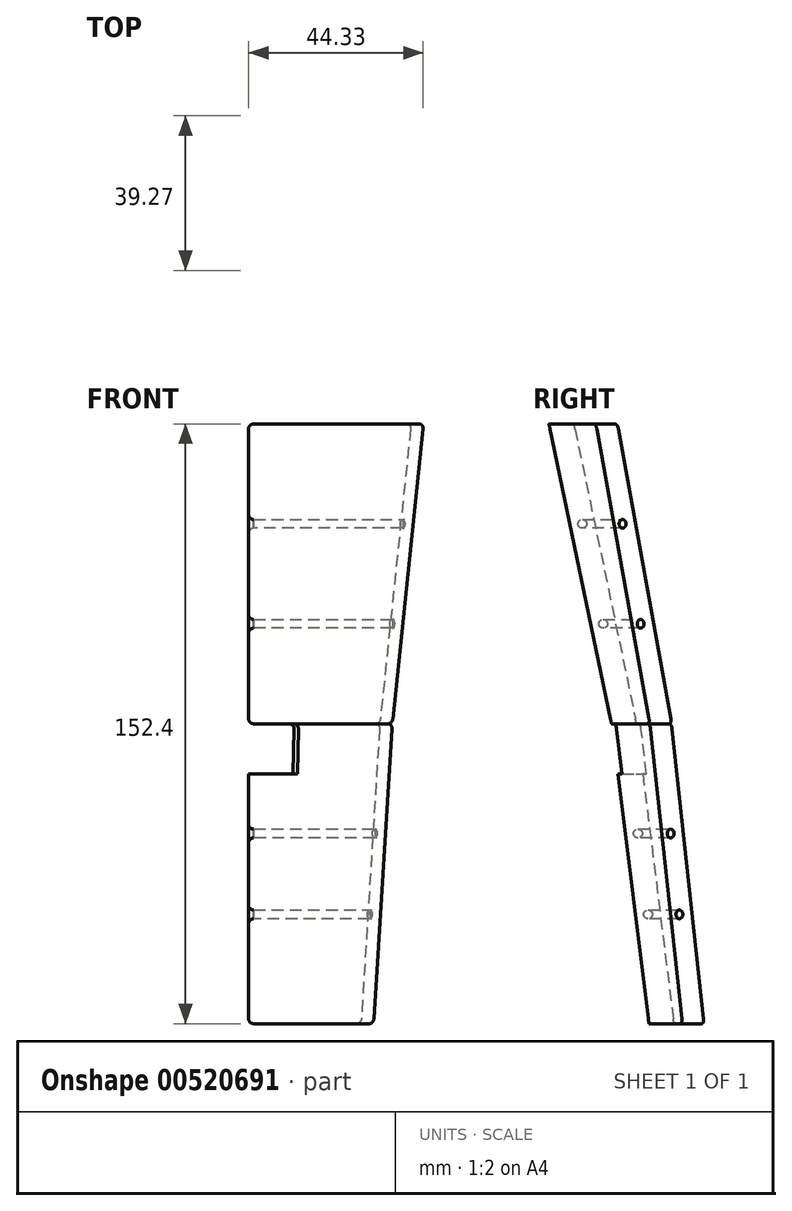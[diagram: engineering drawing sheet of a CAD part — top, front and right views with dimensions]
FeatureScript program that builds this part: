
annotation { "Feature Type Name" : "Feature", "Feature Type Description" : "" }
export const myFeature = defineFeature(function(context is Context, id is Id, definition is map)
    precondition{}
    {
        {
            var Q0;
            Q0=qCreatedBy(makeId("Right.planeOp"),FACE);
            var sketch = newSketch(context, id + "F0", { "sketchPlane" : qUnion([Q0])});
            skLineSegment(sketch, "E0", {"start": v(0, 0) * mm, "end": v(-63.5, 0) * mm});
            skLineSegment(sketch, "E1", {"start": v(0, 0) * mm, "end": v(0, 76.2) * mm});
            skLineSegment(sketch, "E2", {"start": v(0, 76.2) * mm, "end": v(-73.03, 76.2) * mm});
            skLineSegment(sketch, "E3", {"start": v(-73.03, 76.2) * mm, "end": v(-63.5, 0) * mm});
            skSolve(sketch);
        }
        {
            var Q0;
            Q0=makeQuery(id+"F0.imprint","IMPRINT",FACE,{"disambiguationData":[TD([[makeQuery(id+"F0.imprint","IMPRINT",EDGE,{"derivedFrom":sQuery(id+"F0.wireOp",EDGE,"E0")}),-1.0]])]});
            var Q1;
            Q1 = qSketchRegion(id + "F2", true);
            var Q2;
            Q2 = qSketchRegion(id + "F3", true);
            var Q3;
            Q3=sQuery(id+"F0.wireOp",EDGE,"E1");
            revolve(context, id + "F1", {"entities" : qUnion([Q0, Q1, Q2]), "axis" : qUnion([Q3]), "revolveType" : RevolveType.ONE_DIRECTION, "angle" : 30 * degree});
        }
        {
            var Q0;
            Q0=qCreatedBy(makeId("Right.planeOp"),FACE);
            var sketch = newSketch(context, id + "F2", { "sketchPlane" : qUnion([Q0])});
            skLineSegment(sketch, "E4", {"start": v(0, 0) * mm, "end": v(-57.15, 0) * mm});
            skLineSegment(sketch, "E5", {"start": v(0, 0) * mm, "end": v(0, 76.2) * mm});
            skLineSegment(sketch, "E6", {"start": v(-66.68, 76.2) * mm, "end": v(-57.15, 0) * mm});
            skLineSegment(sketch, "E7", {"start": v(-66.68, 76.2) * mm, "end": v(0, 76.2) * mm});
            skSolve(sketch);
        }
        {
            var Q0;
            Q0=qCreatedBy(makeId("Right.planeOp"),FACE);
            var sketch = newSketch(context, id + "F3", { "sketchPlane" : qUnion([Q0])});
            skLineSegment(sketch, "E8", {"start": v(0, 76.2) * mm, "end": v(-73.03, 76.2) * mm});
            skLineSegment(sketch, "E9", {"start": v(0, 76.2) * mm, "end": v(0, 63.5) * mm});
            skLineSegment(sketch, "E10", {"start": v(0, 63.5) * mm, "end": v(-71.44, 63.5) * mm});
            skLineSegment(sketch, "E11", {"start": v(-73.03, 76.2) * mm, "end": v(-71.44, 63.5) * mm});
            skSolve(sketch);
        }
        {
            var Q0;
            Q0 = qSketchRegion(id + "F2", true);
            var Q1;
            Q1=sQuery(id+"F2.wireOp",EDGE,"E5");
            revolve(context, id + "F4", {"operationType" : NewBodyOperationType.REMOVE, "entities" : qUnion([Q0]), "axis" : qUnion([Q1]), "revolveType" : RevolveType.FULL, "oppositeDirection" : true});
        }
        {
            var Q0;
            Q0=makeQuery(id+"F3.imprint","IMPRINT",FACE,{"disambiguationData":[TD([[makeQuery(id+"F3.imprint","IMPRINT",EDGE,{"derivedFrom":sQuery(id+"F3.wireOp",EDGE,"E8")}),1.0]])]});
            var Q1;
            Q1=sQuery(id+"F3.wireOp",EDGE,"E9");
            revolve(context, id + "F5", {"operationType" : NewBodyOperationType.REMOVE, "entities" : qUnion([Q0]), "axis" : qUnion([Q1]), "revolveType" : RevolveType.ONE_DIRECTION, "oppositeDirection" : true, "angle" : 20 * degree});
        }
        {
            var Q0;
            Q0 = qSketchRegion(id + "F3", true);
            var Q1;
            Q1=sQuery(id+"F3.wireOp",EDGE,"E9");
            revolve(context, id + "F6", {"operationType" : NewBodyOperationType.ADD, "entities" : qUnion([Q0]), "axis" : qUnion([Q1]), "revolveType" : RevolveType.ONE_DIRECTION, "oppositeDirection" : true, "angle" : 10 * degree});
        }
        {
            var Q0;
            Q0=qCreatedBy(makeId("Right.planeOp"),FACE);
            var sketch = newSketch(context, id + "F7", { "sketchPlane" : qUnion([Q0])});
            skLineSegment(sketch, "E12", {"start": v(0, 76.2) * mm, "end": v(-66.68, 76.2) * mm});
            skPoint(sketch, "E13", {"position": v(0, 63.5) * mm});
            skLineSegment(sketch, "E14", {"start": v(0, 63.5) * mm, "end": v(-65.09, 63.5) * mm});
            skLineSegment(sketch, "E15", {"start": v(0, 76.2) * mm, "end": v(0, 63.5) * mm});
            skLineSegment(sketch, "E16", {"start": v(-65.09, 63.5) * mm, "end": v(-66.68, 76.2) * mm});
            skSolve(sketch);
        }
        {
            var Q0;
            Q0 = qSketchRegion(id + "F7", true);
            var Q1;
            Q1=sQuery(id+"F3.wireOp",EDGE,"E9");
            revolve(context, id + "F8", {"operationType" : NewBodyOperationType.REMOVE, "entities" : qUnion([Q0]), "axis" : qUnion([Q1]), "revolveType" : RevolveType.FULL, "oppositeDirection" : true});
        }
        {
            var Q0;
            Q0=makeQuery(id+"F6.opRevolve","CAP_EDGE",EDGE,{"disambiguationData":[OSD([sQuery(id+"F3.wireOp",EDGE,"E8")])],"isStart":true});
            var Q1;
            Q1=makeQuery(id+"F6.opRevolve","CAP_EDGE",EDGE,{"disambiguationData":[OSD([sQuery(id+"F3.wireOp",EDGE,"E8")])],"isStart":false});
            var Q2;
            Q2=makeQuery(id+"F5.boolean.opBoolean","COPY",EDGE,{"derivedFrom":makeQuery(id+"F5.opRevolve","CAP_EDGE",EDGE,{"disambiguationData":[OSD([sQuery(id+"F3.wireOp",EDGE,"E8")])],"isStart":false})});
            var Q3;
            Q3=makeQuery(id+"F1.opRevolve","CAP_EDGE",EDGE,{"disambiguationData":[OSD([sQuery(id+"F0.wireOp",EDGE,"E2")])],"isStart":false});
            var Q4;
            Q4=makeQuery(id+"F5.boolean.opBoolean","COPY",EDGE,{"derivedFrom":makeQuery(id+"F5.opRevolve","CAP_EDGE",EDGE,{"disambiguationData":[OSD([sQuery(id+"F3.wireOp",EDGE,"E10")])],"isStart":false})});
            var Q5;
            {var subQ0=sQuery(id+"F3.wireOp",EDGE,"E10");Q5=makeQuery(id+"F6.boolean.opBoolean","SPLIT",EDGE,{"disambiguationData":[topologyDisambiguationEdgeConnected([makeQuery(id+"F5.boolean.opBoolean","COPY",FACE,{"derivedFrom":makeQuery(id+"F5.opRevolve","SWEPT_FACE",FACE,{"disambiguationData":[OSD([subQ0])]})})])],"derivedFrom":makeQuery(id+"F6.opRevolve","CAP_EDGE",EDGE,{"disambiguationData":[OSD([subQ0])],"isStart":false})});}
            var Q6;
            Q6=makeQuery(id+"F1.opRevolve","CAP_EDGE",EDGE,{"disambiguationData":[OSD([sQuery(id+"F0.wireOp",EDGE,"E0")])],"isStart":false});
            var Q7;
            Q7=makeQuery(id+"F1.opRevolve","CAP_EDGE",EDGE,{"disambiguationData":[OSD([sQuery(id+"F0.wireOp",EDGE,"E0")])],"isStart":true});
            fillet(context, id + "F9", {"entities" : qUnion([Q0, Q1, Q2, Q3, Q4, Q5, Q6, Q7]), "radius" : 1.27 * mm, "tangentPropagation" : true, "allowEdgeOverflow" : false});
        }
        {
            var Q0;
            Q0=qCreatedBy(makeId("Right.planeOp"),FACE);
            var sketch = newSketch(context, id + "F10", { "sketchPlane" : qUnion([Q0])});
            skLineSegment(sketch, "E17", {"start": v(0, 76.2) * mm, "end": v(0, 152.4) * mm});
            skLineSegment(sketch, "E18", {"start": v(0, 152.4) * mm, "end": v(-88.9, 152.4) * mm});
            skLineSegment(sketch, "E19", {"start": v(0, 76.2) * mm, "end": v(-73.03, 76.2) * mm});
            skLineSegment(sketch, "E20", {"start": v(-88.9, 152.4) * mm, "end": v(-73.03, 76.2) * mm});
            skSolve(sketch);
        }
        {
            var Q0;
            Q0 = qSketchRegion(id + "F10", true);
            var Q1;
            Q1=sQuery(id+"F10.wireOp",EDGE,"E17");
            revolve(context, id + "F11", {"entities" : qUnion([Q0]), "axis" : qUnion([Q1]), "revolveType" : RevolveType.ONE_DIRECTION, "angle" : 30 * degree});
        }
        {
            var Q0;
            Q0=qCreatedBy(makeId("Right.planeOp"),FACE);
            var sketch = newSketch(context, id + "F12", { "sketchPlane" : qUnion([Q0])});
            skLineSegment(sketch, "E21", {"start": v(0, 0) * mm, "end": v(0, 76.2) * mm});
            skLineSegment(sketch, "E22", {"start": v(0, 76.2) * mm, "end": v(0, 152.4) * mm});
            skLineSegment(sketch, "E23", {"start": v(0, 152.4) * mm, "end": v(-82.55, 152.4) * mm});
            skLineSegment(sketch, "E24", {"start": v(0, 76.2) * mm, "end": v(-66.68, 76.2) * mm});
            skLineSegment(sketch, "E25", {"start": v(-66.68, 76.2) * mm, "end": v(-82.55, 152.4) * mm});
            skSolve(sketch);
        }
        {
            var Q0;
            Q0 = qSketchRegion(id + "F12", true);
            var Q1;
            Q1=sQuery(id+"F12.wireOp",EDGE,"E22");
            revolve(context, id + "F13", {"operationType" : NewBodyOperationType.REMOVE, "entities" : qUnion([Q0]), "axis" : qUnion([Q1]), "revolveType" : RevolveType.FULL, "oppositeDirection" : true});
        }
        {
            var Q0;
            Q0=qCreatedBy(makeId("Right.planeOp"),FACE);
            var sketch = newSketch(context, id + "F14", { "sketchPlane" : qUnion([Q0])});
            skLineSegment(sketch, "E26", {"start": v(-71.44, 63.5) * mm, "end": v(-65.09, 63.5) * mm});
            skLineSegment(sketch, "E27", {"start": v(-65.09, 63.5) * mm, "end": v(-66.68, 76.2) * mm});
            skLineSegment(sketch, "E28", {"start": v(-73.03, 76.2) * mm, "end": v(-71.44, 63.5) * mm});
            skLineSegment(sketch, "E29", {"start": v(-73.03, 76.2) * mm, "end": v(-66.68, 76.2) * mm});
            skLineSegment(sketch, "E30", {"start": v(-65.09, 63.5) * mm, "end": v(-71.44, 63.5) * mm});
            skSolve(sketch);
        }
        {
            var Q0;
            Q0=qCreatedBy(makeId("Right.planeOp"),FACE);
            var sketch = newSketch(context, id + "F15", { "sketchPlane" : qUnion([Q0])});
            skLineSegment(sketch, "E31", {"start": v(0, 0) * mm, "end": v(0, 76) * mm});
            skSolve(sketch);
        }
        {
            var Q0;
            Q0=makeQuery(id+"F14.imprint","IMPRINT",FACE,{"disambiguationData":[TD([[makeQuery(id+"F14.imprint","IMPRINT",EDGE,{"derivedFrom":sQuery(id+"F14.wireOp",EDGE,"E27")}),1.0]])]});
            var Q1;
            Q1=sQuery(id+"F15.wireOp",EDGE,"E31");
            revolve(context, id + "F16", {"operationType" : NewBodyOperationType.ADD, "entities" : qUnion([Q0]), "axis" : qUnion([Q1]), "revolveType" : RevolveType.ONE_DIRECTION, "angle" : 20 * degree});
        }
        {
            var Q0;
            Q0 = qSketchRegion(id + "F14", true);
            var Q1;
            Q1=sQuery(id+"F15.wireOp",EDGE,"E31");
            revolve(context, id + "F17", {"operationType" : NewBodyOperationType.REMOVE, "entities" : qUnion([Q0]), "axis" : qUnion([Q1]), "revolveType" : RevolveType.ONE_DIRECTION, "angle" : 10 * degree});
        }
        {
            var Q0;
            Q0=makeQuery(id+"F16.opRevolve","CAP_EDGE",EDGE,{"disambiguationData":[OSD([sQuery(id+"F14.wireOp",EDGE,"E30")])],"isStart":false});
            var Q1;
            Q1=makeQuery(id+"F17.boolean.opBoolean","COPY",EDGE,{"derivedFrom":makeQuery(id+"F17.opRevolve","CAP_EDGE",EDGE,{"disambiguationData":[OSD([sQuery(id+"F14.wireOp",EDGE,"E30")])],"isStart":false})});
            var Q2;
            Q2=makeQuery(id+"F17.boolean.opBoolean","COPY",EDGE,{"derivedFrom":makeQuery(id+"F17.opRevolve","CAP_EDGE",EDGE,{"disambiguationData":[OSD([sQuery(id+"F14.wireOp",EDGE,"E29")])],"isStart":false})});
            var Q3;
            Q3=makeQuery(id+"F16.opRevolve","CAP_EDGE",EDGE,{"disambiguationData":[OSD([sQuery(id+"F14.wireOp",EDGE,"E29")])],"isStart":false});
            var Q4;
            Q4=makeQuery(id+"F11.opRevolve","CAP_EDGE",EDGE,{"disambiguationData":[OSD([sQuery(id+"F10.wireOp",EDGE,"E19")])],"isStart":false});
            var Q5;
            Q5=makeQuery(id+"F17.boolean.opBoolean","COPY",EDGE,{"derivedFrom":makeQuery(id+"F17.opRevolve","CAP_EDGE",EDGE,{"disambiguationData":[OSD([sQuery(id+"F14.wireOp",EDGE,"E29")])],"isStart":true})});
            var Q6;
            Q6=makeQuery(id+"F11.opRevolve","CAP_EDGE",EDGE,{"disambiguationData":[OSD([sQuery(id+"F10.wireOp",EDGE,"E18")])],"isStart":true});
            var Q7;
            Q7=makeQuery(id+"F11.opRevolve","CAP_EDGE",EDGE,{"disambiguationData":[OSD([sQuery(id+"F10.wireOp",EDGE,"E18")])],"isStart":false});
            fillet(context, id + "F18", {"entities" : qUnion([Q0, Q1, Q2, Q3, Q4, Q5, Q6, Q7]), "radius" : 1.27 * mm, "tangentPropagation" : true, "allowEdgeOverflow" : false});
        }
        {
            var Q0;
            Q0=qCreatedBy(makeId("Right.planeOp"),FACE);
            var sketch = newSketch(context, id + "F19", { "sketchPlane" : qUnion([Q0])});
            skPoint(sketch, "E32", {"position": v(-66.32, 48.32) * mm});
            skPoint(sketch, "E33", {"position": v(-63.75, 27.78) * mm});
            skCircle(sketch, "E34", {"center": v(-66.32, 48.32) * mm, "radius": 1.11 * mm});
            skCircle(sketch, "E35", {"center": v(-63.75, 27.78) * mm, "radius": 1.11 * mm});
            skLineSegment(sketch, "E36", {"start": v(-88.9, 152.4) * mm, "end": v(-82.55, 152.4) * mm});
            skPoint(sketch, "E37", {"position": v(-80.43, 127) * mm});
            skPoint(sketch, "E38", {"position": v(-75.14, 101.6) * mm});
            skCircle(sketch, "E39", {"center": v(-75.14, 101.6) * mm, "radius": 1.11 * mm});
            skCircle(sketch, "E40", {"center": v(-80.43, 127) * mm, "radius": 1.11 * mm});
            skSolve(sketch);
        }
        {
            var Q0;
            Q0 = qSketchRegion(id + "F19", true);
            var Q1;
            Q1=sQuery(id+"F15.wireOp",EDGE,"E31");
            revolve(context, id + "F20", {"operationType" : NewBodyOperationType.REMOVE, "entities" : qUnion([Q0]), "axis" : qUnion([Q1]), "revolveType" : RevolveType.FULL, "oppositeDirection" : true});
        }
        {
            var Q0;
            Q0=makeQuery(id+"F20.boolean.opBoolean","INTERSECT",EDGE,{"derivedFrom":[makeQuery(id+"F16.boolean.opBoolean","MERGE",FACE,{"derivedFrom":[makeQuery(id+"F11.opRevolve","CAP_FACE",FACE,{"disambiguationData":[OSD([sQuery(id+"F10.wireOp",EDGE,"E17"),sQuery(id+"F10.wireOp",EDGE,"E18"),sQuery(id+"F10.wireOp",EDGE,"E19"),sQuery(id+"F10.wireOp",EDGE,"E20")])],"isStart":true}),makeQuery(id+"F16.opRevolve","CAP_FACE",FACE,{"disambiguationData":[OSD([sQuery(id+"F14.wireOp",EDGE,"E27"),sQuery(id+"F14.wireOp",EDGE,"E28"),sQuery(id+"F14.wireOp",EDGE,"E29"),sQuery(id+"F14.wireOp",EDGE,"E30")])],"isStart":true})]}),makeQuery(id+"F20.opRevolve","SWEPT_FACE",FACE,{"disambiguationData":[OSD([sQuery(id+"F19.wireOp",EDGE,"E40")])]})]});
            var Q1;
            Q1=makeQuery(id+"F20.boolean.opBoolean","INTERSECT",EDGE,{"derivedFrom":[makeQuery(id+"F16.boolean.opBoolean","MERGE",FACE,{"derivedFrom":[makeQuery(id+"F11.opRevolve","CAP_FACE",FACE,{"disambiguationData":[OSD([sQuery(id+"F10.wireOp",EDGE,"E17"),sQuery(id+"F10.wireOp",EDGE,"E18"),sQuery(id+"F10.wireOp",EDGE,"E19"),sQuery(id+"F10.wireOp",EDGE,"E20")])],"isStart":true}),makeQuery(id+"F16.opRevolve","CAP_FACE",FACE,{"disambiguationData":[OSD([sQuery(id+"F14.wireOp",EDGE,"E27"),sQuery(id+"F14.wireOp",EDGE,"E28"),sQuery(id+"F14.wireOp",EDGE,"E29"),sQuery(id+"F14.wireOp",EDGE,"E30")])],"isStart":true})]}),makeQuery(id+"F20.opRevolve","SWEPT_FACE",FACE,{"disambiguationData":[OSD([sQuery(id+"F19.wireOp",EDGE,"E39")])]})]});
            var Q2;
            Q2=makeQuery(id+"F20.boolean.opBoolean","INTERSECT",EDGE,{"derivedFrom":[makeQuery(id+"F6.boolean.opBoolean","MERGE",FACE,{"derivedFrom":[makeQuery(id+"F1.opRevolve","CAP_FACE",FACE,{"disambiguationData":[OSD([sQuery(id+"F0.wireOp",EDGE,"E0"),sQuery(id+"F0.wireOp",EDGE,"E1"),sQuery(id+"F0.wireOp",EDGE,"E2"),sQuery(id+"F0.wireOp",EDGE,"E3")])],"isStart":true}),makeQuery(id+"F6.opRevolve","CAP_FACE",FACE,{"disambiguationData":[OSD([sQuery(id+"F3.wireOp",EDGE,"E8"),sQuery(id+"F3.wireOp",EDGE,"E9"),sQuery(id+"F3.wireOp",EDGE,"E10"),sQuery(id+"F3.wireOp",EDGE,"E11")])],"isStart":true})]}),makeQuery(id+"F20.opRevolve","SWEPT_FACE",FACE,{"disambiguationData":[OSD([sQuery(id+"F19.wireOp",EDGE,"E34")])]})]});
            var Q3;
            Q3=makeQuery(id+"F20.boolean.opBoolean","INTERSECT",EDGE,{"derivedFrom":[makeQuery(id+"F6.boolean.opBoolean","MERGE",FACE,{"derivedFrom":[makeQuery(id+"F1.opRevolve","CAP_FACE",FACE,{"disambiguationData":[OSD([sQuery(id+"F0.wireOp",EDGE,"E0"),sQuery(id+"F0.wireOp",EDGE,"E1"),sQuery(id+"F0.wireOp",EDGE,"E2"),sQuery(id+"F0.wireOp",EDGE,"E3")])],"isStart":true}),makeQuery(id+"F6.opRevolve","CAP_FACE",FACE,{"disambiguationData":[OSD([sQuery(id+"F3.wireOp",EDGE,"E8"),sQuery(id+"F3.wireOp",EDGE,"E9"),sQuery(id+"F3.wireOp",EDGE,"E10"),sQuery(id+"F3.wireOp",EDGE,"E11")])],"isStart":true})]}),makeQuery(id+"F20.opRevolve","SWEPT_FACE",FACE,{"disambiguationData":[OSD([sQuery(id+"F19.wireOp",EDGE,"E35")])]})]});
            var Q4;
            Q4=makeQuery(id+"F20.boolean.opBoolean","INTERSECT",EDGE,{"derivedFrom":[makeQuery(id+"F11.opRevolve","CAP_FACE",FACE,{"disambiguationData":[OSD([sQuery(id+"F10.wireOp",EDGE,"E17"),sQuery(id+"F10.wireOp",EDGE,"E18"),sQuery(id+"F10.wireOp",EDGE,"E19"),sQuery(id+"F10.wireOp",EDGE,"E20")])],"isStart":false}),makeQuery(id+"F20.opRevolve","SWEPT_FACE",FACE,{"disambiguationData":[OSD([sQuery(id+"F19.wireOp",EDGE,"E40")])]})]});
            var Q5;
            Q5=makeQuery(id+"F20.boolean.opBoolean","INTERSECT",EDGE,{"derivedFrom":[makeQuery(id+"F11.opRevolve","CAP_FACE",FACE,{"disambiguationData":[OSD([sQuery(id+"F10.wireOp",EDGE,"E17"),sQuery(id+"F10.wireOp",EDGE,"E18"),sQuery(id+"F10.wireOp",EDGE,"E19"),sQuery(id+"F10.wireOp",EDGE,"E20")])],"isStart":false}),makeQuery(id+"F20.opRevolve","SWEPT_FACE",FACE,{"disambiguationData":[OSD([sQuery(id+"F19.wireOp",EDGE,"E39")])]})]});
            var Q6;
            Q6=makeQuery(id+"F20.boolean.opBoolean","INTERSECT",EDGE,{"derivedFrom":[makeQuery(id+"F1.opRevolve","CAP_FACE",FACE,{"disambiguationData":[OSD([sQuery(id+"F0.wireOp",EDGE,"E0"),sQuery(id+"F0.wireOp",EDGE,"E1"),sQuery(id+"F0.wireOp",EDGE,"E2"),sQuery(id+"F0.wireOp",EDGE,"E3")])],"isStart":false}),makeQuery(id+"F20.opRevolve","SWEPT_FACE",FACE,{"disambiguationData":[OSD([sQuery(id+"F19.wireOp",EDGE,"E34")])]})]});
            var Q7;
            Q7=makeQuery(id+"F20.boolean.opBoolean","INTERSECT",EDGE,{"derivedFrom":[makeQuery(id+"F1.opRevolve","CAP_FACE",FACE,{"disambiguationData":[OSD([sQuery(id+"F0.wireOp",EDGE,"E0"),sQuery(id+"F0.wireOp",EDGE,"E1"),sQuery(id+"F0.wireOp",EDGE,"E2"),sQuery(id+"F0.wireOp",EDGE,"E3")])],"isStart":false}),makeQuery(id+"F20.opRevolve","SWEPT_FACE",FACE,{"disambiguationData":[OSD([sQuery(id+"F19.wireOp",EDGE,"E35")])]})]});
            fillet(context, id + "F21", {"entities" : qUnion([Q0, Q1, Q2, Q3, Q4, Q5, Q6, Q7]), "radius" : 1.27 * mm, "tangentPropagation" : true, "allowEdgeOverflow" : false});
        }
    });
